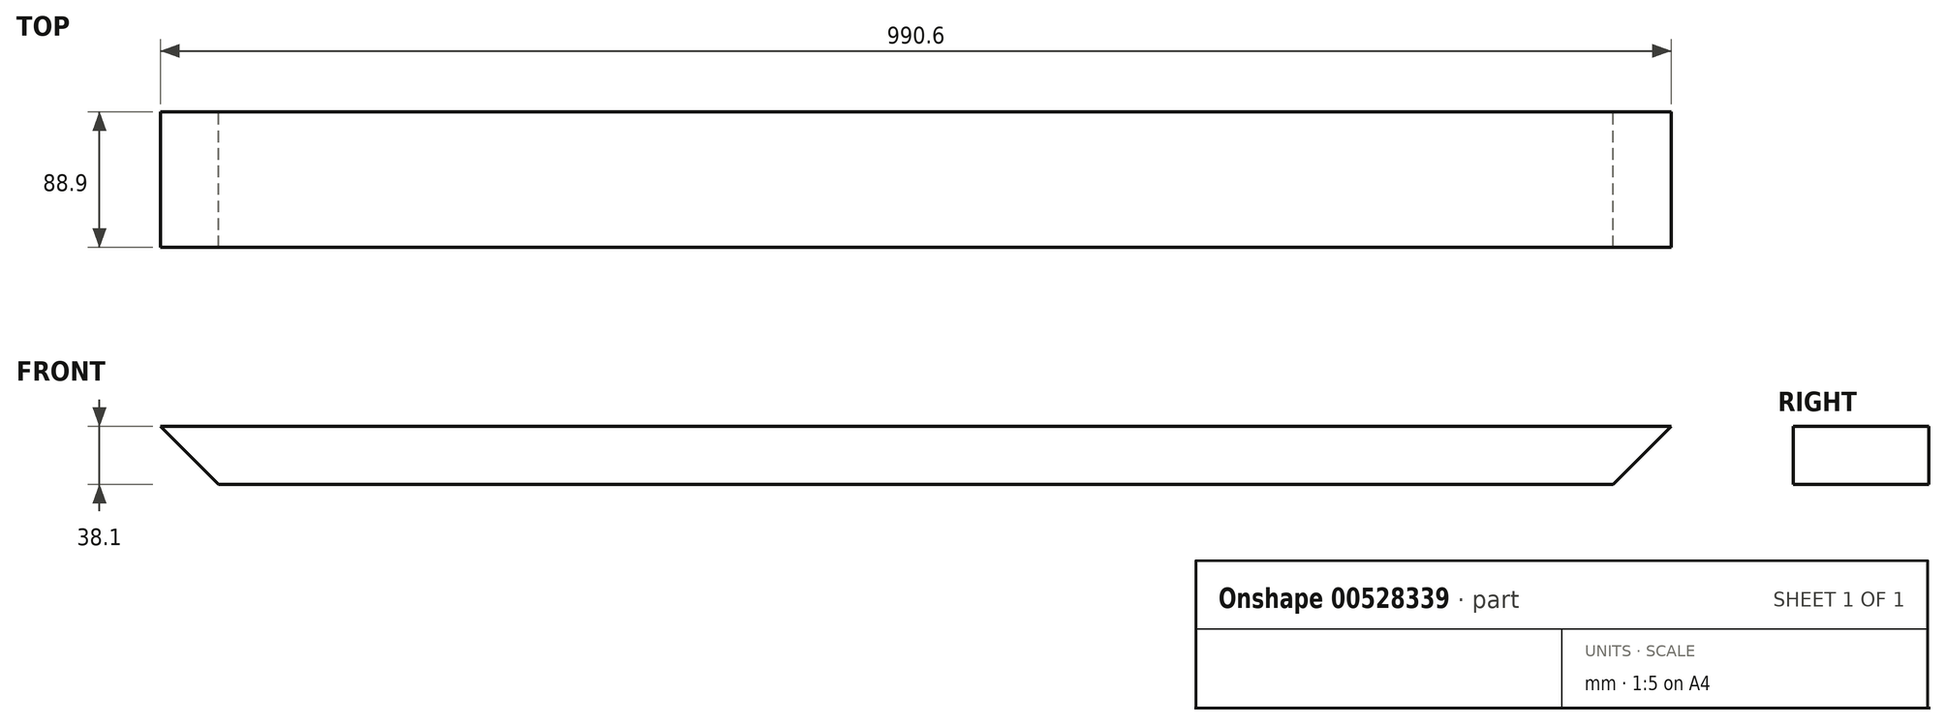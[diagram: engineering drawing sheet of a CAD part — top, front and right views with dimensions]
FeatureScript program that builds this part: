
annotation { "Feature Type Name" : "Feature", "Feature Type Description" : "" }
export const myFeature = defineFeature(function(context is Context, id is Id, definition is map)
    precondition{}
    {
        {
            var Q0;
            Q0=qCreatedBy(makeId("Front.planeOp"),FACE);
            var sketch = newSketch(context, id + "F0", { "sketchPlane" : qUnion([Q0])});
            skLineSegment(sketch, "E0", {"start": v(-68.63, 38.1) * mm, "end": v(921.97, 38.1) * mm});
            skLineSegment(sketch, "E1", {"start": v(921.97, 38.1) * mm, "end": v(921.97, 0) * mm, "construction": true});
            skLineSegment(sketch, "E2", {"start": v(921.97, 38.1) * mm, "end": v(883.87, 0) * mm});
            skLineSegment(sketch, "E3", {"start": v(-68.63, 38.1) * mm, "end": v(-68.63, -73.09) * mm, "construction": true});
            skLineSegment(sketch, "E4", {"start": v(883.87, 0) * mm, "end": v(-30.53, 0) * mm});
            skLineSegment(sketch, "E5", {"start": v(-30.53, 0) * mm, "end": v(-68.63, 38.1) * mm});
            skSolve(sketch);
        }
        {
            var Q0;
            Q0=makeQuery(id+"F0.imprint","IMPRINT",FACE,{"disambiguationData":[TD([[makeQuery(id+"F0.imprint","IMPRINT",EDGE,{"derivedFrom":sQuery(id+"F0.wireOp",EDGE,"E0")}),-1.0]])]});
            extrude(context, id + "F1", {"entities" : qUnion([Q0]), "depth" : 88.9 * mm, "offsetDistance" : 25.4 * mm});
        }
    });
